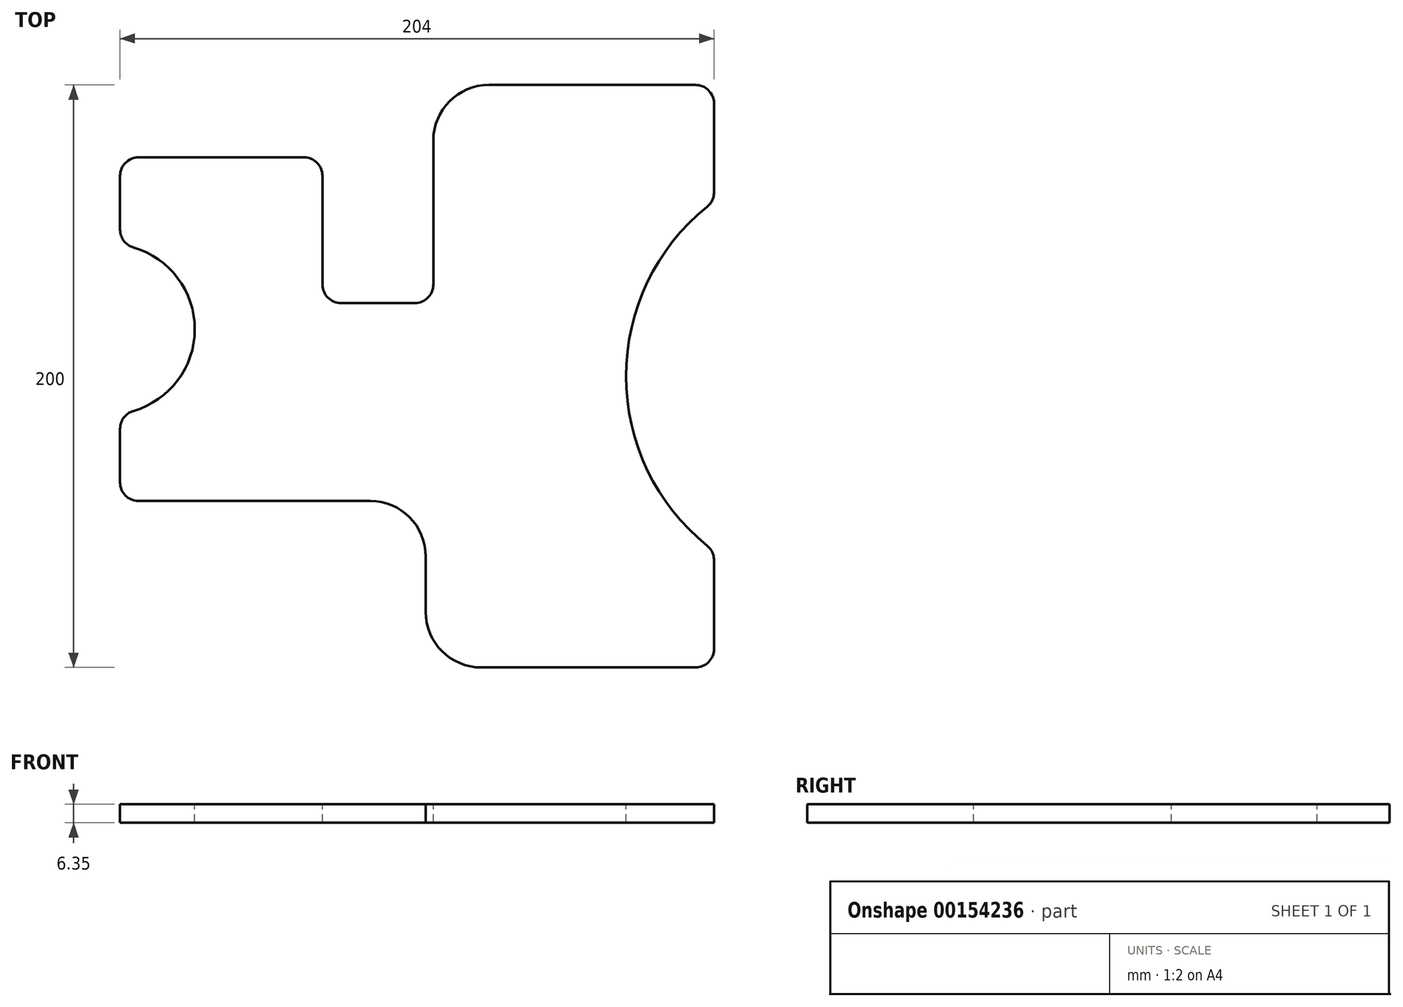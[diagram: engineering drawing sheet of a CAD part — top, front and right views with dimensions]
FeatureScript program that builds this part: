
annotation { "Feature Type Name" : "Feature", "Feature Type Description" : "" }
export const myFeature = defineFeature(function(context is Context, id is Id, definition is map)
    precondition{}
    {
        {
            var Q0;
            Q0=qCreatedBy(makeId("Top.planeOp"),FACE);
            var sketch = newSketch(context, id + "F0", { "sketchPlane" : qUnion([Q0])});
            skLineSegment(sketch, "E0", {"start": v(-98.65, -42.85) * mm, "end": v(-19.05, -42.85) * mm});
            skLineSegment(sketch, "E1", {"start": v(0, -61.9) * mm, "end": v(0, -80.95) * mm});
            skLineSegment(sketch, "E2", {"start": v(19.05, -100) * mm, "end": v(92.65, -100) * mm});
            skLineSegment(sketch, "E3", {"start": v(99, -93.65) * mm, "end": v(99, -63.12) * mm});
            skLineSegment(sketch, "E4", {"start": v(99, 63.12) * mm, "end": v(99, 93.65) * mm});
            skLineSegment(sketch, "E5", {"start": v(92.65, 100) * mm, "end": v(21.65, 100) * mm});
            skLineSegment(sketch, "E6", {"start": v(-41.85, 75.15) * mm, "end": v(-98.65, 75.15) * mm});
            skLineSegment(sketch, "E7", {"start": v(-105, 68.8) * mm, "end": v(-105, 50.3) * mm});
            skLineSegment(sketch, "E8", {"start": v(-105, -18) * mm, "end": v(-105, -36.5) * mm});
            skArc(sketch, "E9", {"start": v(96.63, 58.17) * mm, "mid": v(68.78, 0) * mm, "end": v(96.63, -58.17) * mm});
            skArc(sketch, "E10", {"start": v(-100.42, -11.91) * mm, "mid": v(-79.34, 16.15) * mm, "end": v(-100.42, 44.21) * mm});
            skPoint(sketch, "E11.visualSharp", {"position": v(-105, 75.15) * mm});
            skArc(sketch, "E11.filletArc", {"start": v(-98.65, 75.15) * mm, "mid": v(-103.14, 73.3) * mm, "end": v(-105, 68.8) * mm});
            skPoint(sketch, "E12.visualSharp", {"position": v(-105, 45.15) * mm});
            skArc(sketch, "E12.filletArc", {"start": v(-105, 50.3) * mm, "mid": v(-103.73, 46.5) * mm, "end": v(-100.42, 44.21) * mm});
            skPoint(sketch, "E13.visualSharp", {"position": v(-105, -12.85) * mm});
            skArc(sketch, "E13.filletArc", {"start": v(-100.42, -11.91) * mm, "mid": v(-103.73, -14.2) * mm, "end": v(-105, -18) * mm});
            skPoint(sketch, "E14.visualSharp", {"position": v(-105, -42.85) * mm});
            skArc(sketch, "E14.filletArc", {"start": v(-105, -36.5) * mm, "mid": v(-103.14, -41) * mm, "end": v(-98.65, -42.85) * mm});
            skPoint(sketch, "E15.visualSharp", {"position": v(99, 100) * mm});
            skArc(sketch, "E15.filletArc", {"start": v(99, 93.65) * mm, "mid": v(97.14, 98.14) * mm, "end": v(92.65, 100) * mm});
            skPoint(sketch, "E16.visualSharp", {"position": v(99, 60) * mm});
            skArc(sketch, "E16.filletArc", {"start": v(96.63, 58.17) * mm, "mid": v(98.38, 60.38) * mm, "end": v(99, 63.12) * mm});
            skPoint(sketch, "E17.visualSharp", {"position": v(99, -60) * mm});
            skArc(sketch, "E17.filletArc", {"start": v(99, -63.12) * mm, "mid": v(98.38, -60.38) * mm, "end": v(96.63, -58.17) * mm});
            skPoint(sketch, "E18.visualSharp", {"position": v(99, -100) * mm});
            skArc(sketch, "E18.filletArc", {"start": v(92.65, -100) * mm, "mid": v(97.14, -98.14) * mm, "end": v(99, -93.65) * mm});
            skPoint(sketch, "E19.visualSharp", {"position": v(0, 100) * mm});
            skPoint(sketch, "E20.visualSharp", {"position": v(0, -100) * mm});
            skArc(sketch, "E20.filletArc", {"start": v(0, -80.95) * mm, "mid": v(5.58, -94.42) * mm, "end": v(19.05, -100) * mm});
            skPoint(sketch, "E21.visualSharp", {"position": v(0, 75.15) * mm});
            skPoint(sketch, "E22.visualSharp", {"position": v(0, -42.85) * mm});
            skArc(sketch, "E22.filletArc", {"start": v(0, -61.9) * mm, "mid": v(-5.58, -48.43) * mm, "end": v(-19.05, -42.85) * mm});
            skLineSegment(sketch, "E23", {"start": v(-35.5, 68.8) * mm, "end": v(-35.5, 31.5) * mm});
            skLineSegment(sketch, "E24", {"start": v(-29.15, 25.15) * mm, "end": v(-3.75, 25.15) * mm});
            skLineSegment(sketch, "E25", {"start": v(2.6, 31.5) * mm, "end": v(2.6, 75.15) * mm});
            skLineSegment(sketch, "E26", {"start": v(2.6, 80.95) * mm, "end": v(2.6, 75.15) * mm});
            skPoint(sketch, "E27.visualSharp", {"position": v(2.6, 100) * mm});
            skArc(sketch, "E27.filletArc", {"start": v(21.65, 100) * mm, "mid": v(8.18, 94.42) * mm, "end": v(2.6, 80.95) * mm});
            skPoint(sketch, "E28.visualSharp", {"position": v(-35.5, 75.15) * mm});
            skArc(sketch, "E28.filletArc", {"start": v(-35.5, 68.8) * mm, "mid": v(-37.36, 73.3) * mm, "end": v(-41.85, 75.15) * mm});
            skPoint(sketch, "E29.visualSharp", {"position": v(-35.5, 25.15) * mm});
            skArc(sketch, "E29.filletArc", {"start": v(-35.5, 31.5) * mm, "mid": v(-33.64, 27) * mm, "end": v(-29.15, 25.15) * mm});
            skPoint(sketch, "E30.visualSharp", {"position": v(2.6, 25.15) * mm});
            skArc(sketch, "E30.filletArc", {"start": v(-3.75, 25.15) * mm, "mid": v(0.74, 27) * mm, "end": v(2.6, 31.5) * mm});
            skSolve(sketch);
        }
        {
            var Q0;
            Q0=qSketchRegion(id+"F0",true);
            extrude(context, id + "F1", {"entities" : qUnion([Q0]), "oppositeDirection" : true, "depth" : 6.35 * mm});
        }
    });
